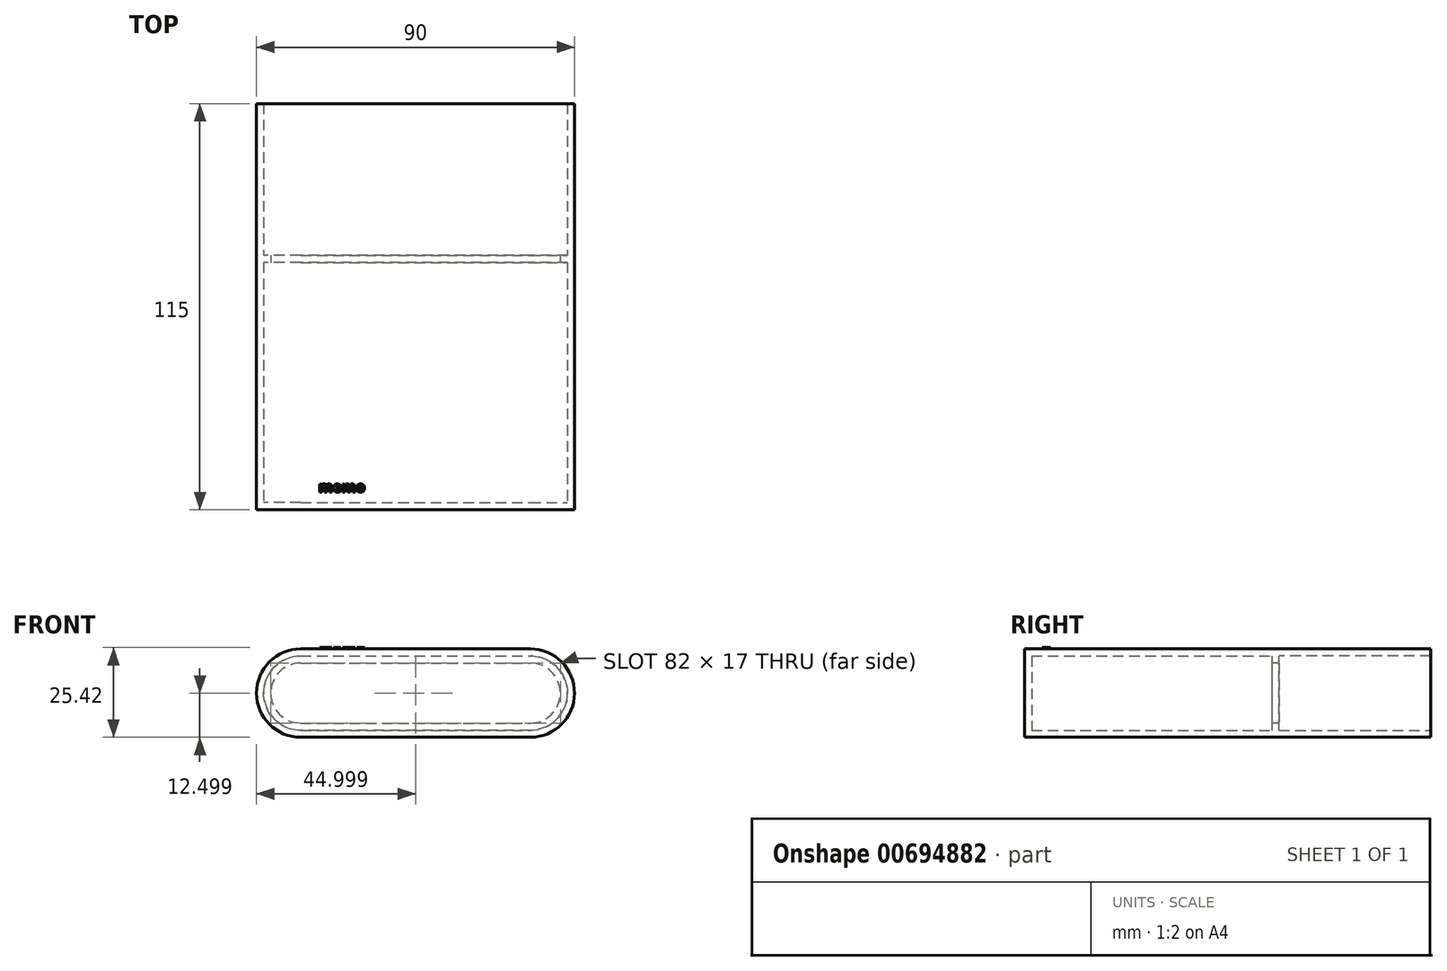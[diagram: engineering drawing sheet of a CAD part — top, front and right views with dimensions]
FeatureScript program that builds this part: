
annotation { "Feature Type Name" : "Feature", "Feature Type Description" : "" }
export const myFeature = defineFeature(function(context is Context, id is Id, definition is map)
    precondition{}
    {
        {
            var Q0;
            Q0=qCreatedBy(makeId("Front.planeOp"),FACE);
            var sketch = newSketch(context, id + "F0", { "sketchPlane" : qUnion([Q0])});
            skPoint(sketch, "E0.middle", {"position": v(-2.04, -12.42) * mm});
            skLineSegment(sketch, "E1.bottom", {"start": v(-34.54, 0.08) * mm, "end": v(30.46, 0.08) * mm});
            skLineSegment(sketch, "E1.top", {"start": v(-34.54, -24.92) * mm, "end": v(30.46, -24.92) * mm});
            skLineSegment(sketch, "E2.bottom", {"start": v(-34.54, -1.92) * mm, "end": v(30.46, -1.92) * mm});
            skLineSegment(sketch, "E2.top", {"start": v(-34.54, -22.92) * mm, "end": v(30.46, -22.92) * mm});
            skArc(sketch, "E3", {"start": v(30.46, -24.92) * mm, "mid": v(42.96, -12.42) * mm, "end": v(30.46, 0.08) * mm});
            skArc(sketch, "E4", {"start": v(-34.54, -1.92) * mm, "mid": v(-45.04, -12.42) * mm, "end": v(-34.54, -22.92) * mm});
            skArc(sketch, "E5", {"start": v(-34.54, 0.08) * mm, "mid": v(-47.04, -12.42) * mm, "end": v(-34.54, -24.92) * mm});
            skArc(sketch, "E6", {"start": v(30.46, -22.92) * mm, "mid": v(40.96, -12.42) * mm, "end": v(30.46, -1.92) * mm});
            skLineSegment(sketch, "E7", {"start": v(-34.54, -1.92) * mm, "end": v(-34.54, -3.92) * mm});
            skLineSegment(sketch, "E8", {"start": v(-34.54, -3.92) * mm, "end": v(-34.54, -4.42) * mm});
            skLineSegment(sketch, "E9", {"start": v(-34.54, -4.42) * mm, "end": v(30.46, -4.42) * mm});
            skLineSegment(sketch, "E10", {"start": v(-34.54, -3.92) * mm, "end": v(30.46, -3.92) * mm});
            skLineSegment(sketch, "E11", {"start": v(30.46, -22.92) * mm, "end": v(30.46, -20.92) * mm});
            skLineSegment(sketch, "E12", {"start": v(30.46, -20.92) * mm, "end": v(30.46, -20.42) * mm});
            skLineSegment(sketch, "E13", {"start": v(30.46, -20.42) * mm, "end": v(-34.54, -20.42) * mm});
            skLineSegment(sketch, "E14", {"start": v(-34.54, -20.92) * mm, "end": v(30.46, -20.92) * mm});
            skArc(sketch, "E15", {"start": v(-34.54, -4.42) * mm, "mid": v(-42.54, -12.42) * mm, "end": v(-34.54, -20.42) * mm});
            skArc(sketch, "E16", {"start": v(-34.54, -3.92) * mm, "mid": v(-43.04, -12.42) * mm, "end": v(-34.54, -20.92) * mm});
            skArc(sketch, "E17", {"start": v(30.46, -20.42) * mm, "mid": v(38.46, -12.42) * mm, "end": v(30.46, -4.42) * mm});
            skArc(sketch, "E18", {"start": v(30.46, -20.92) * mm, "mid": v(38.96, -12.42) * mm, "end": v(30.46, -3.92) * mm});
            skSolve(sketch);
        }
        {
            var Q0;
            Q0 = qSketchRegion(id + "F0", true);
            extrude(context, id + "F1", {"entities" : qUnion([Q0]), "oppositeDirection" : true, "depth" : 115 * mm, "offsetDistance" : 25 * mm});
        }
        {
            var Q0;
            Q0=makeQuery(id+"F0.imprint","IMPRINT",FACE,{"disambiguationData":[TD([[makeQuery(id+"F0.imprint","IMPRINT",EDGE,{"derivedFrom":sQuery(id+"F0.wireOp",EDGE,"E2.top")}),1.0]])]});
            var Q1;
            Q1=makeQuery(id+"F0.imprint","IMPRINT",FACE,{"disambiguationData":[TD([[makeQuery(id+"F0.imprint","IMPRINT",EDGE,{"derivedFrom":sQuery(id+"F0.wireOp",EDGE,"E2.bottom")}),-1.0]])]});
            var Q2;
            Q2=makeQuery(id+"F0.imprint","IMPRINT",FACE,{"disambiguationData":[TD([[makeQuery(id+"F0.imprint","IMPRINT",EDGE,{"derivedFrom":sQuery(id+"F0.wireOp",EDGE,"E8")}),1.0]])]});
            var Q3;
            Q3=makeQuery(id+"F0.imprint","IMPRINT",FACE,{"disambiguationData":[TD([[makeQuery(id+"F0.imprint","IMPRINT",EDGE,{"derivedFrom":sQuery(id+"F0.wireOp",EDGE,"E8")}),-1.0]])]});
            var Q4;
            Q4=makeQuery(id+"F0.imprint","IMPRINT",FACE,{"disambiguationData":[TD([[makeQuery(id+"F0.imprint","IMPRINT",EDGE,{"derivedFrom":sQuery(id+"F0.wireOp",EDGE,"E9")}),-1.0]])]});
            extrude(context, id + "F2", {"entities" : qUnion([Q0, Q1, Q2, Q3, Q4]), "operationType" : NewBodyOperationType.ADD, "oppositeDirection" : true, "depth" : 2 * mm, "offsetDistance" : 25 * mm});
        }
        {
            var Q0;
            Q0=qCreatedBy(makeId("Front.planeOp"),FACE);
            cPlane(context, id + "F3", {"entities" : qUnion([Q0]), "cplaneType" : CPlaneType.OFFSET, "offset" : 70 * mm, "oppositeDirection" : true, "width" : 150 * mm, "height" : 150 * mm});
        }
        {
            var Q0;
            Q0=qCreatedBy(id+"F3.planeOp",FACE);
            var sketch = newSketch(context, id + "F4", { "sketchPlane" : qUnion([Q0])});
            skPoint(sketch, "E19.middle", {"position": v(-2.04, -12.42) * mm});
            skLineSegment(sketch, "E20.bottom", {"start": v(-34.54, 0.08) * mm, "end": v(30.46, 0.08) * mm});
            skLineSegment(sketch, "E20.top", {"start": v(-34.54, -24.92) * mm, "end": v(30.46, -24.92) * mm});
            skLineSegment(sketch, "E21.bottom", {"start": v(-34.54, -1.92) * mm, "end": v(30.46, -1.92) * mm});
            skLineSegment(sketch, "E21.top", {"start": v(-34.54, -22.92) * mm, "end": v(30.46, -22.92) * mm});
            skArc(sketch, "E22", {"start": v(30.46, -24.92) * mm, "mid": v(42.96, -12.42) * mm, "end": v(30.46, 0.08) * mm});
            skArc(sketch, "E23", {"start": v(-34.54, -1.92) * mm, "mid": v(-45.04, -12.42) * mm, "end": v(-34.54, -22.92) * mm});
            skArc(sketch, "E24", {"start": v(-34.54, 0.08) * mm, "mid": v(-47.04, -12.42) * mm, "end": v(-34.54, -24.92) * mm});
            skArc(sketch, "E25", {"start": v(30.46, -22.92) * mm, "mid": v(40.96, -12.42) * mm, "end": v(30.46, -1.92) * mm});
            skLineSegment(sketch, "E26", {"start": v(-34.54, -1.92) * mm, "end": v(-34.54, -3.92) * mm});
            skLineSegment(sketch, "E27", {"start": v(-34.54, -3.92) * mm, "end": v(-34.54, -4.42) * mm});
            skLineSegment(sketch, "E28", {"start": v(-40.6, -20.46) * mm, "end": v(24.4, -20.46) * mm});
            skLineSegment(sketch, "E29", {"start": v(-34.54, -3.92) * mm, "end": v(30.46, -3.92) * mm});
            skLineSegment(sketch, "E30", {"start": v(30.46, -22.92) * mm, "end": v(30.46, -20.92) * mm});
            skLineSegment(sketch, "E31", {"start": v(30.46, -20.92) * mm, "end": v(30.46, -20.42) * mm});
            skLineSegment(sketch, "E32", {"start": v(30.46, -20.42) * mm, "end": v(-34.54, -20.42) * mm});
            skLineSegment(sketch, "E33", {"start": v(-34.54, -20.92) * mm, "end": v(30.46, -20.92) * mm});
            skArc(sketch, "E34", {"start": v(-34.54, -4.42) * mm, "mid": v(-42.54, -12.42) * mm, "end": v(-34.54, -20.42) * mm});
            skArc(sketch, "E35", {"start": v(-34.54, -3.92) * mm, "mid": v(-43.04, -12.42) * mm, "end": v(-34.54, -20.92) * mm});
            skArc(sketch, "E36", {"start": v(30.46, -20.42) * mm, "mid": v(38.46, -12.42) * mm, "end": v(30.46, -4.42) * mm});
            skArc(sketch, "E37", {"start": v(30.46, -20.92) * mm, "mid": v(38.96, -12.42) * mm, "end": v(30.46, -3.92) * mm});
            skSolve(sketch);
        }
        {
            var Q0;
            Q0=makeQuery(id+"F4.imprint","IMPRINT",FACE,{"disambiguationData":[TD([[makeQuery(id+"F4.imprint","IMPRINT",EDGE,{"derivedFrom":sQuery(id+"F4.wireOp",EDGE,"E21.bottom")}),-1.0]])]});
            var Q1;
            Q1=makeQuery(id+"F4.imprint","IMPRINT",FACE,{"disambiguationData":[TD([[makeQuery(id+"F4.imprint","IMPRINT",EDGE,{"derivedFrom":sQuery(id+"F4.wireOp",EDGE,"E21.top")}),1.0]])]});
            extrude(context, id + "F5", {"entities" : qUnion([Q0, Q1]), "operationType" : NewBodyOperationType.ADD, "oppositeDirection" : true, "depth" : 2 * mm, "offsetDistance" : 25 * mm});
        }
        {
            var Q0;
            Q0=qCreatedBy(makeId("Top.planeOp"),FACE);
            var sketch = newSketch(context, id + "F6", { "sketchPlane" : qUnion([Q0])});
            skText(sketch, "E38", { "text": "memo", "fontName": "OpenSans-Bold.ttf"});
            const initialGuessF6  = {"E38": [-0.02952, 0.005, 1, 0, 0.003]};
            skSetInitialGuess(sketch, initialGuessF6);
            skSolve(sketch);
        }
        {
            var Q0;
            Q0 = qSketchRegion(id + "F6", true);
            extrude(context, id + "F7", {"entities" : qUnion([Q0]), "operationType" : NewBodyOperationType.ADD, "depth" : 0.5 * mm, "offsetDistance" : 25 * mm});
        }
    });
